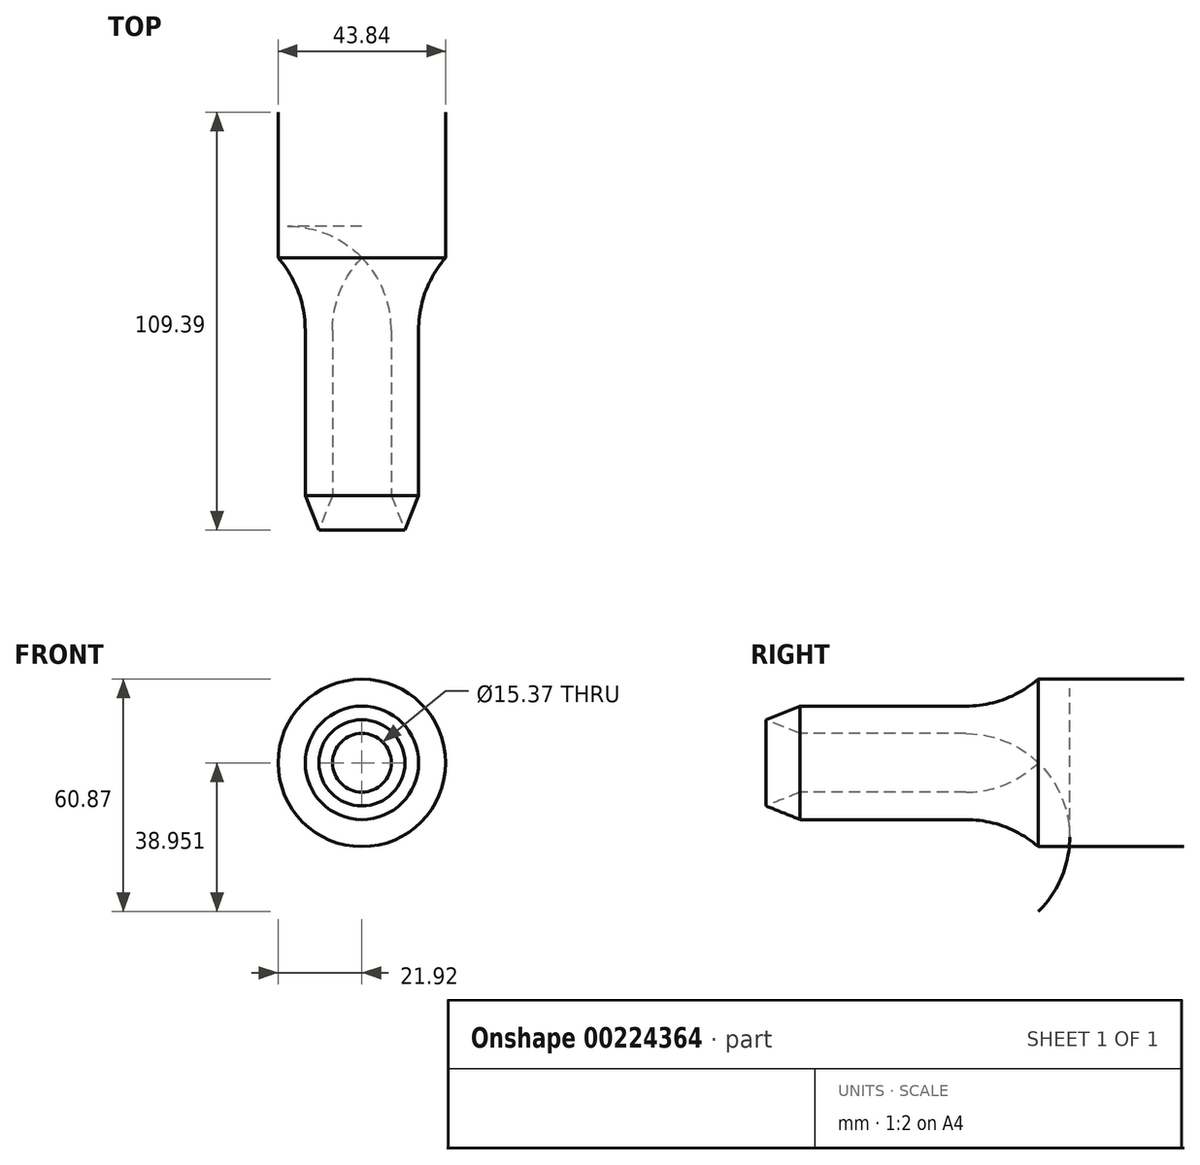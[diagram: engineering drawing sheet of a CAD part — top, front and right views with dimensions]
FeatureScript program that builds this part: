
annotation { "Feature Type Name" : "Feature", "Feature Type Description" : "" }
export const myFeature = defineFeature(function(context is Context, id is Id, definition is map)
    precondition{}
    {
        {
            var Q0;
            Q0=qCreatedBy(makeId("Right.planeOp"),FACE);
            var sketch = newSketch(context, id + "F0", { "sketchPlane" : qUnion([Q0])});
            skLineSegment(sketch, "E0", {"start": v(-71.29, 0) * mm, "end": v(-62.3, 3.59) * mm});
            skLineSegment(sketch, "E1", {"start": v(-71.29, 0) * mm, "end": v(-62.3, -3.57) * mm});
            skLineSegment(sketch, "E2", {"start": v(-62.3, 3.59) * mm, "end": v(-18.93, 3.59) * mm});
            skLineSegment(sketch, "E3", {"start": v(-62.3, -3.57) * mm, "end": v(-18.93, -3.57) * mm});
            skArc(sketch, "E4", {"start": v(-18.93, 3.59) * mm, "mid": v(-8.83, 5.41) * mm, "end": v(0, 10.66) * mm});
            skArc(sketch, "E5", {"start": v(0, -11.26) * mm, "mid": v(-8.72, -5.57) * mm, "end": v(-18.93, -3.57) * mm});
            skLineSegment(sketch, "E6", {"start": v(0, 10.66) * mm, "end": v(38.1, 10.66) * mm});
            skLineSegment(sketch, "E7", {"start": v(0, -11.26) * mm, "end": v(38.1, -11.26) * mm});
            skArc(sketch, "E8", {"start": v(38.1, -11.26) * mm, "mid": v(49.06, -0.3) * mm, "end": v(38.1, 10.66) * mm});
            skSolve(sketch);
        }
        {
            var Q0;
            Q0=makeQuery(id+"F0.imprint","IMPRINT",FACE,{"disambiguationData":[TD([[makeQuery(id+"F0.imprint","IMPRINT",EDGE,{"derivedFrom":sQuery(id+"F0.wireOp",EDGE,"E0")}),-1.0]])]});
            var Q1;
            Q1=makeQuery(id+"F0.imprint","IMPRINT",FACE,{"disambiguationData":[TD([[makeQuery(id+"F0.imprint","IMPRINT",EDGE,{"derivedFrom":sQuery(id+"F0.wireOp",EDGE,"E0")}),-1.0]])]});
            var Q2;
            Q2=sQuery(id+"F0.wireOp",EDGE,"E7");
            revolve(context, id + "F1", {"entities" : qUnion([Q0, Q1]), "axis" : qUnion([Q2]), "revolveType" : RevolveType.FULL});
        }
    });
